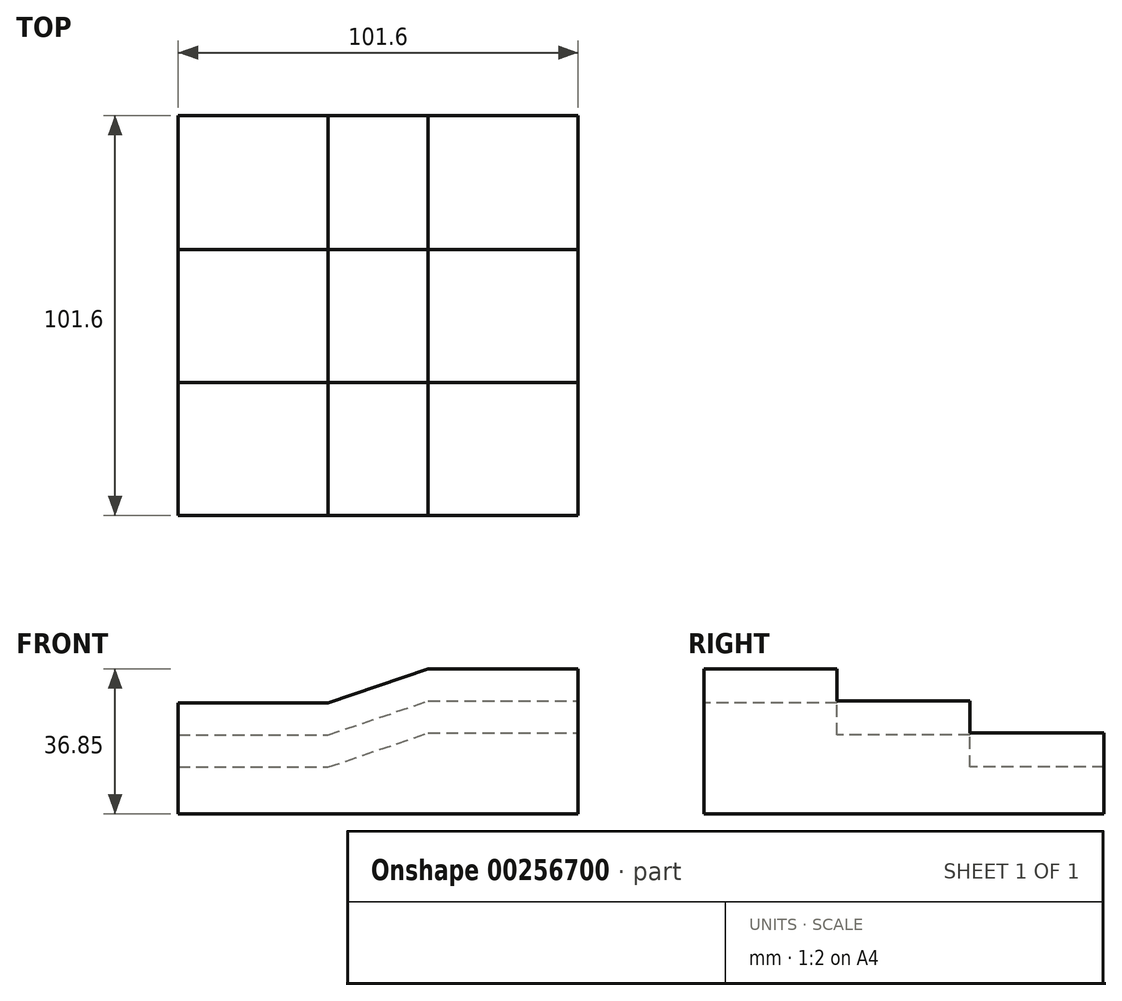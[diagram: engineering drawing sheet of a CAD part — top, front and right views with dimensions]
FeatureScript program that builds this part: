
annotation { "Feature Type Name" : "Feature", "Feature Type Description" : "" }
export const myFeature = defineFeature(function(context is Context, id is Id, definition is map)
    precondition{}
    {
        {
            var Q0;
            Q0=qCreatedBy(makeId("Front.planeOp"),FACE);
            var sketch = newSketch(context, id + "F0", { "sketchPlane" : qUnion([Q0])});
            skLineSegment(sketch, "E0.right", {"start": v(77.31, -20.08) * mm, "end": v(77.31, 24.93) * mm});
            skLineSegment(sketch, "E1", {"start": v(-24.29, -20.08) * mm, "end": v(-24.29, 24.93) * mm});
            skLineSegment(sketch, "E2", {"start": v(-24.29, 24.93) * mm, "end": v(77.31, 24.93) * mm});
            skLineSegment(sketch, "E3", {"start": v(-24.29, -8.15) * mm, "end": v(13.81, -8.15) * mm});
            skLineSegment(sketch, "E4", {"start": v(13.81, -8.15) * mm, "end": v(39.21, 0.46) * mm});
            skLineSegment(sketch, "E5", {"start": v(39.21, 0.46) * mm, "end": v(77.31, 0.46) * mm});
            skLineSegment(sketch, "E6", {"start": v(-24.29, 0) * mm, "end": v(13.81, 0) * mm});
            skLineSegment(sketch, "E7", {"start": v(13.81, 0) * mm, "end": v(39.21, 8.62) * mm});
            skLineSegment(sketch, "E8", {"start": v(39.21, 8.62) * mm, "end": v(77.31, 8.62) * mm});
            skLineSegment(sketch, "E9", {"start": v(-24.29, 8.15) * mm, "end": v(13.81, 8.15) * mm});
            skLineSegment(sketch, "E10", {"start": v(13.81, 8.15) * mm, "end": v(39.21, 16.77) * mm});
            skLineSegment(sketch, "E11", {"start": v(39.21, 16.77) * mm, "end": v(77.31, 16.77) * mm});
            skLineSegment(sketch, "E12", {"start": v(-24.29, 16.3) * mm, "end": v(13.81, 16.3) * mm});
            skLineSegment(sketch, "E13", {"start": v(13.81, 16.3) * mm, "end": v(39.21, 24.93) * mm});
            skLineSegment(sketch, "E14", {"start": v(39.21, 24.93) * mm, "end": v(77.31, 24.93) * mm});
            skLineSegment(sketch, "E15", {"start": v(-24.29, 0) * mm, "end": v(-24.29, -8.15) * mm});
            skLineSegment(sketch, "E16", {"start": v(-24.29, -20.08) * mm, "end": v(77.31, -20.08) * mm});
            skSolve(sketch);
        }
        {
            var Q0;
            {var subQ0=sQuery(id+"F0.wireOp",EDGE,"E3");Q0=makeQuery(id+"F0.imprint","IMPRINT",FACE,{"disambiguationData":[TD([[makeQuery(id+"F0.imprint","IMPRINT",EDGE,{"derivedFrom":subQ0}),-1.0]])]});}
            extrude(context, id + "F1", {"entities" : qUnion([Q0]), "oppositeDirection" : true, "depth" : 101.6 * mm});
        }
        {
            var Q0;
            Q0=makeQuery(id+"F0.imprint","IMPRINT",FACE,{"disambiguationData":[TD([[makeQuery(id+"F0.imprint","IMPRINT",EDGE,{"derivedFrom":sQuery(id+"F0.wireOp",EDGE,"E3")}),1.0]])]});
            extrude(context, id + "F2", {"entities" : qUnion([Q0]), "operationType" : NewBodyOperationType.ADD, "oppositeDirection" : true, "depth" : 67.56 * mm});
        }
        {
            var Q0;
            {var subQ1=sQuery(id+"F0.wireOp",EDGE,"E6");Q0=makeQuery(id+"F0.imprint","IMPRINT",FACE,{"disambiguationData":[TD([[makeQuery(id+"F0.imprint","IMPRINT",EDGE,{"derivedFrom":subQ1}),1.0]])]});}
            extrude(context, id + "F3", {"entities" : qUnion([Q0]), "operationType" : NewBodyOperationType.ADD, "oppositeDirection" : true, "depth" : 33.78 * mm});
        }
    });
